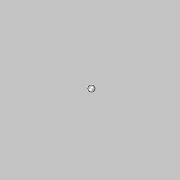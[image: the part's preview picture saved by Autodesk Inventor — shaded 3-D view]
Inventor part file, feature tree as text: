
AUTODESK INVENTOR PART (.ipt)
format: ipt  version: 2017 (Build 210142000, 142)  size: 107,008 bytes
history: native  units: mm
features: other x10, sketch x3, sweep x1, extrude x1, pattern_circular x1
ambient origin geometry x7: Origin, YZ Plane, XZ Plane, X Axis, Y Axis, Z Axis, Center Point
bodies: Solid1 (feature_tree), Solid2 (feature_tree)
feature tree (16):
  other  "Table"
  other  "CableLadderBendKHJZP-150"
  other  "CableLadderBendKHJZP-200"
  other  "CableLadderBendKHJZP-300"
  other  "CableLadderBendKHJZP-400"
  other  "CableLadderBendKHJZP-500"
  other  "CableLadderBendKHJZP-600"
  other  "CableLadderBendKHJZP-800"
  other  "CableLadderBendKHJZP-1000"
  sweep  "Sweep1"
  extrude  "Extrusion2"  Depth=18.0mm
  pattern_circular  "Circular Pattern1"  Count=300  [1 undecoded]
  other  "XY Ground Plane"
  sketch  "Sketch4"  dims[d0=55.0mm d1=18.0mm]
  sketch  "Sketch5"  dims[d5=30.0mm d6=18.0mm d7=3000.0mm d8=0.0mm]
  sketch  "Sketch6"  dims[d17=0.0mm d18=0.0mm d20=30.0mm d21=90.0deg d24=272.0mm d25=452.0mm d26=0.0mm]
note: 1 required parameter value undecoded (feature->parameter linkage not recoverable at this tier; creation-order binding heuristic only, values carry confidence <= 0.55)
